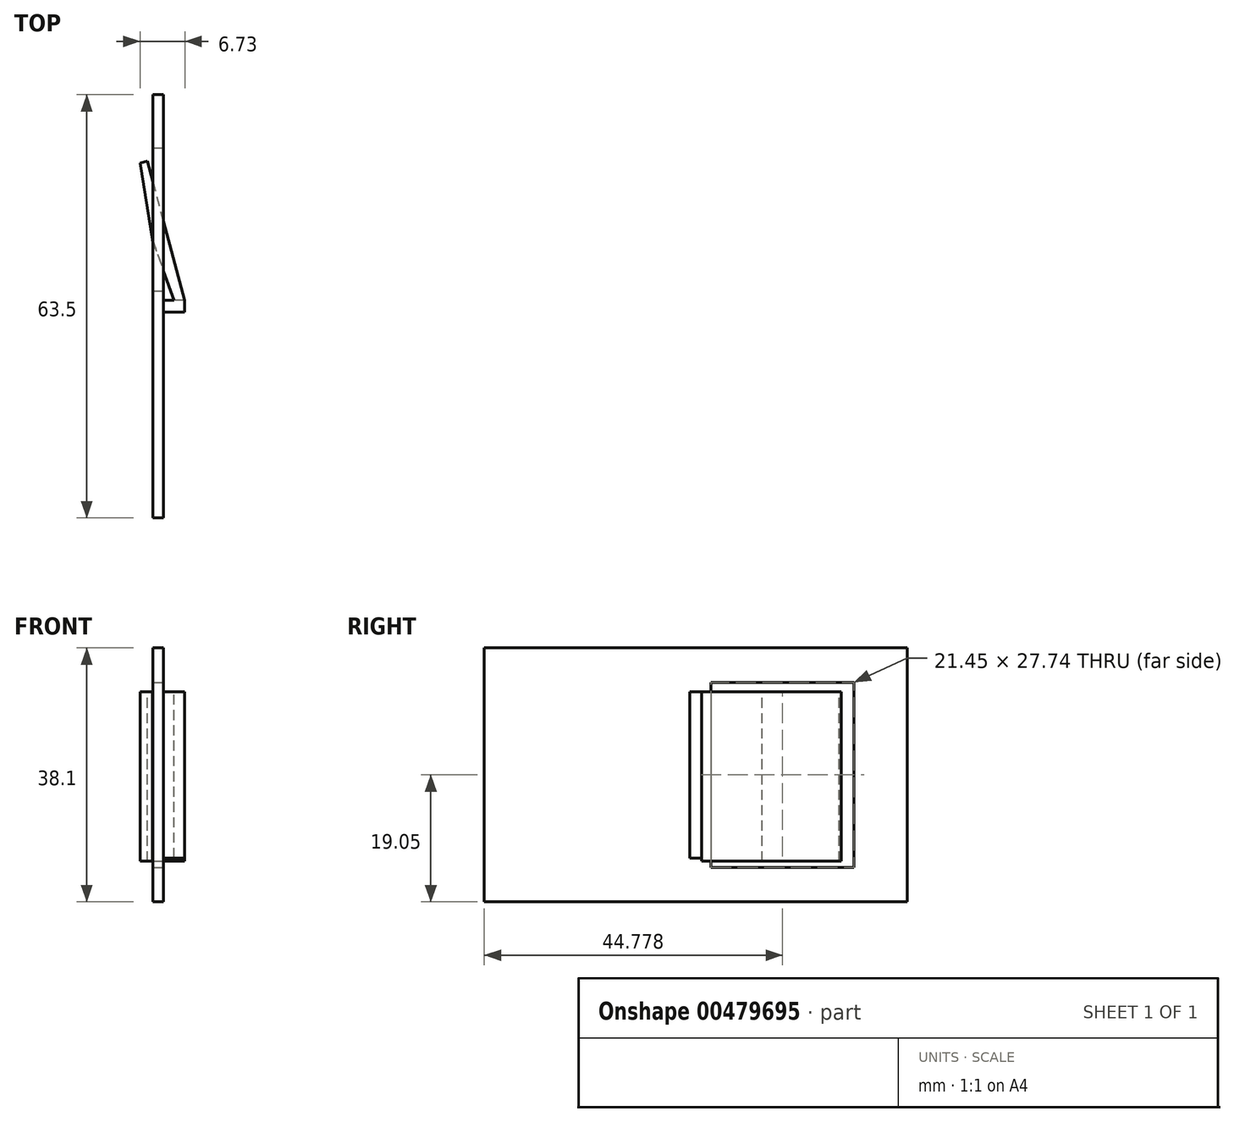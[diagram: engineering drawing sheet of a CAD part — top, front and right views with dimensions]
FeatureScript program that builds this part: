
annotation { "Feature Type Name" : "Feature", "Feature Type Description" : "" }
export const myFeature = defineFeature(function(context is Context, id is Id, definition is map)
    precondition{}
    {
        {
            var Q0;
            Q0=qCreatedBy(makeId("Front.planeOp"),FACE);
            var sketch = newSketch(context, id + "F0", { "sketchPlane" : qUnion([Q0])});
            skLineSegment(sketch, "E0.bottom", {"start": v(0.8, 19.05) * mm, "end": v(-0.8, 19.05) * mm});
            skLineSegment(sketch, "E0.top", {"start": v(0.8, -19.05) * mm, "end": v(-0.8, -19.05) * mm});
            skLineSegment(sketch, "E0.left", {"start": v(0.8, 19.05) * mm, "end": v(0.8, -19.05) * mm});
            skLineSegment(sketch, "E0.right", {"start": v(-0.8, 19.05) * mm, "end": v(-0.8, -19.05) * mm});
            skPoint(sketch, "E0.middle", {"position": v(0, 0) * mm});
            skSolve(sketch);
        }
        {
            var Q0;
            Q0 = qSketchRegion(id + "F0", true);
            extrude(context, id + "F1", {"entities" : qUnion([Q0]), "depth" : 63.5 * mm});
        }
        {
            var Q0;
            Q0=makeQuery(id+"F1.opExtrude","SWEPT_FACE",FACE,{"disambiguationData":[OSD([sQuery(id+"F0.wireOp",EDGE,"E0.left")])]});
            var sketch = newSketch(context, id + "F2", { "sketchPlane" : qUnion([Q0])});
            skLineSegment(sketch, "E1.bottom", {"start": v(-30.86, 12.46) * mm, "end": v(-32.64, 12.46) * mm});
            skLineSegment(sketch, "E1.top", {"start": v(-30.86, -12.46) * mm, "end": v(-32.64, -12.46) * mm});
            skLineSegment(sketch, "E1.left", {"start": v(-30.86, 12.46) * mm, "end": v(-30.86, -12.46) * mm});
            skLineSegment(sketch, "E1.right", {"start": v(-32.64, 12.46) * mm, "end": v(-32.64, -12.46) * mm});
            skPoint(sketch, "E1.middle", {"position": v(-31.75, 0) * mm});
            skPoint(sketch, "E1.middle.positionSnap0", {"position": v(-31.75, 19.05) * mm});
            skPoint(sketch, "E1.centerSnap0", {"position": v(-31.75, 19.05) * mm});
            skSolve(sketch);
        }
        {
            var Q0;
            Q0 = qSketchRegion(id + "F2", true);
            extrude(context, id + "F3", {"entities" : qUnion([Q0]), "operationType" : NewBodyOperationType.ADD, "depth" : 3.17 * mm});
        }
        {
            var Q0;
            Q0=makeQuery(id+"F3.opExtrude","SWEPT_FACE",FACE,{"disambiguationData":[OSD([sQuery(id+"F2.wireOp",EDGE,"E1.bottom")])]});
            var sketch = newSketch(context, id + "F4", { "sketchPlane" : qUnion([Q0])});
            skLineSegment(sketch, "E2", {"start": v(3.97, -30.86) * mm, "end": v(-1.63, -9.95) * mm});
            skLineSegment(sketch, "E3", {"start": v(-0.9, -21.77) * mm, "end": v(2.38, -30.86) * mm});
            skLineSegment(sketch, "E4", {"start": v(2.38, -30.86) * mm, "end": v(3.97, -30.86) * mm});
            skLineSegment(sketch, "E5", {"start": v(-1.63, -9.95) * mm, "end": v(-2.76, -10.25) * mm});
            skLineSegment(sketch, "E6", {"start": v(-2.76, -10.25) * mm, "end": v(-0.9, -21.77) * mm});
            skSolve(sketch);
        }
        {
            var Q0;
            Q0=makeQuery(id+"F1.opExtrude","SWEPT_FACE",FACE,{"disambiguationData":[OSD([sQuery(id+"F0.wireOp",EDGE,"E0.left")])]});
            var sketch = newSketch(context, id + "F5", { "sketchPlane" : qUnion([Q0])});
            skLineSegment(sketch, "E7.bottom", {"start": v(-8, 13.87) * mm, "end": v(-29.45, 13.87) * mm});
            skLineSegment(sketch, "E7.top", {"start": v(-8, -13.87) * mm, "end": v(-29.45, -13.87) * mm});
            skLineSegment(sketch, "E7.left", {"start": v(-8, 13.87) * mm, "end": v(-8, -13.87) * mm});
            skLineSegment(sketch, "E7.right", {"start": v(-29.45, 13.87) * mm, "end": v(-29.45, -13.87) * mm});
            skPoint(sketch, "E7.middle", {"position": v(-18.72, 0) * mm});
            skSolve(sketch);
        }
        {
            var Q0;
            Q0 = qSketchRegion(id + "F5", true);
            extrude(context, id + "F6", {"entities" : qUnion([Q0]), "operationType" : NewBodyOperationType.REMOVE, "oppositeDirection" : true, "depth" : 25.4 * mm, "hasSecondDirection" : true, "secondDirectionOppositeDirection" : false, "secondDirectionDepth" : 25.4 * mm});
        }
        {
            var Q0;
            Q0 = qSketchRegion(id + "F4", true);
            extrude(context, id + "F7", {"entities" : qUnion([Q0]), "operationType" : NewBodyOperationType.ADD, "oppositeDirection" : true, "depth" : 25.4 * mm});
        }
    });
